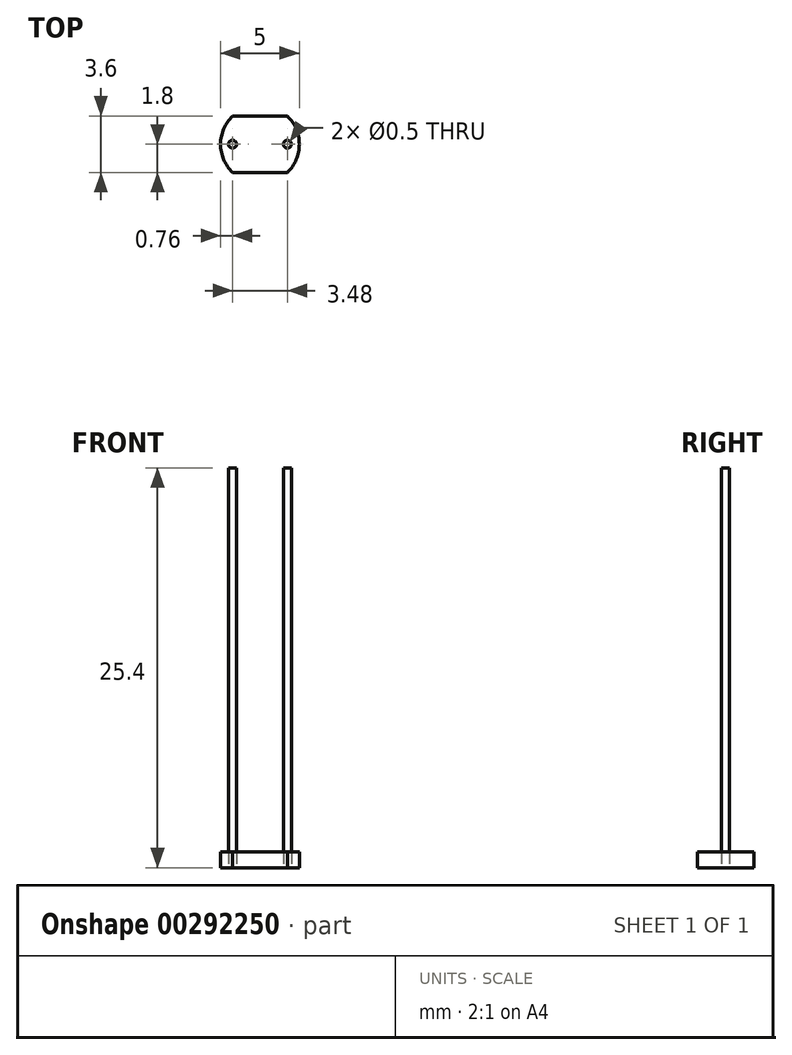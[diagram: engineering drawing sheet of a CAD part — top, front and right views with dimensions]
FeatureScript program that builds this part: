
annotation { "Feature Type Name" : "Feature", "Feature Type Description" : "" }
export const myFeature = defineFeature(function(context is Context, id is Id, definition is map)
    precondition{}
    {
        {
            var Q0;
            Q0=qCreatedBy(makeId("Top.planeOp"),FACE);
            var sketch = newSketch(context, id + "F0", { "sketchPlane" : qUnion([Q0])});
            skArc(sketch, "E0", {"start": v(-1.74, 1.8) * mm, "mid": v(-2.5, 0) * mm, "end": v(-1.74, -1.8) * mm});
            skLineSegment(sketch, "E1.bottom", {"start": v(1.74, -1.8) * mm, "end": v(-1.74, -1.8) * mm});
            skLineSegment(sketch, "E1.top", {"start": v(1.74, 1.8) * mm, "end": v(-1.74, 1.8) * mm});
            skArc(sketch, "E2.trimOffspring", {"start": v(1.74, -1.8) * mm, "mid": v(2.5, 0) * mm, "end": v(1.74, 1.8) * mm});
            skCircle(sketch, "E3", {"center": v(-1.74, 0) * mm, "radius": 0.25 * mm});
            skCircle(sketch, "E4", {"center": v(1.74, 0) * mm, "radius": 0.25 * mm});
            skSolve(sketch);
        }
        {
            var Q0;
            Q0 = qSketchRegion(id + "F0", true);
            extrude(context, id + "F1", {"entities" : qUnion([Q0]), "depth" : 1 * mm});
        }
        {
            var Q0;
            Q0=makeQuery(id+"F0.imprint","IMPRINT",FACE,{"disambiguationData":[TD([[makeQuery(id+"F0.imprint","IMPRINT",EDGE,{"derivedFrom":sQuery(id+"F0.wireOp",EDGE,"E4")}),1.0]])]});
            var Q1;
            Q1=makeQuery(id+"F0.imprint","IMPRINT",FACE,{"disambiguationData":[TD([[makeQuery(id+"F0.imprint","IMPRINT",EDGE,{"derivedFrom":sQuery(id+"F0.wireOp",EDGE,"E3")}),1.0]])]});
            extrude(context, id + "F2", {"entities" : qUnion([Q0, Q1]), "depth" : 25.4 * mm});
        }
    });
